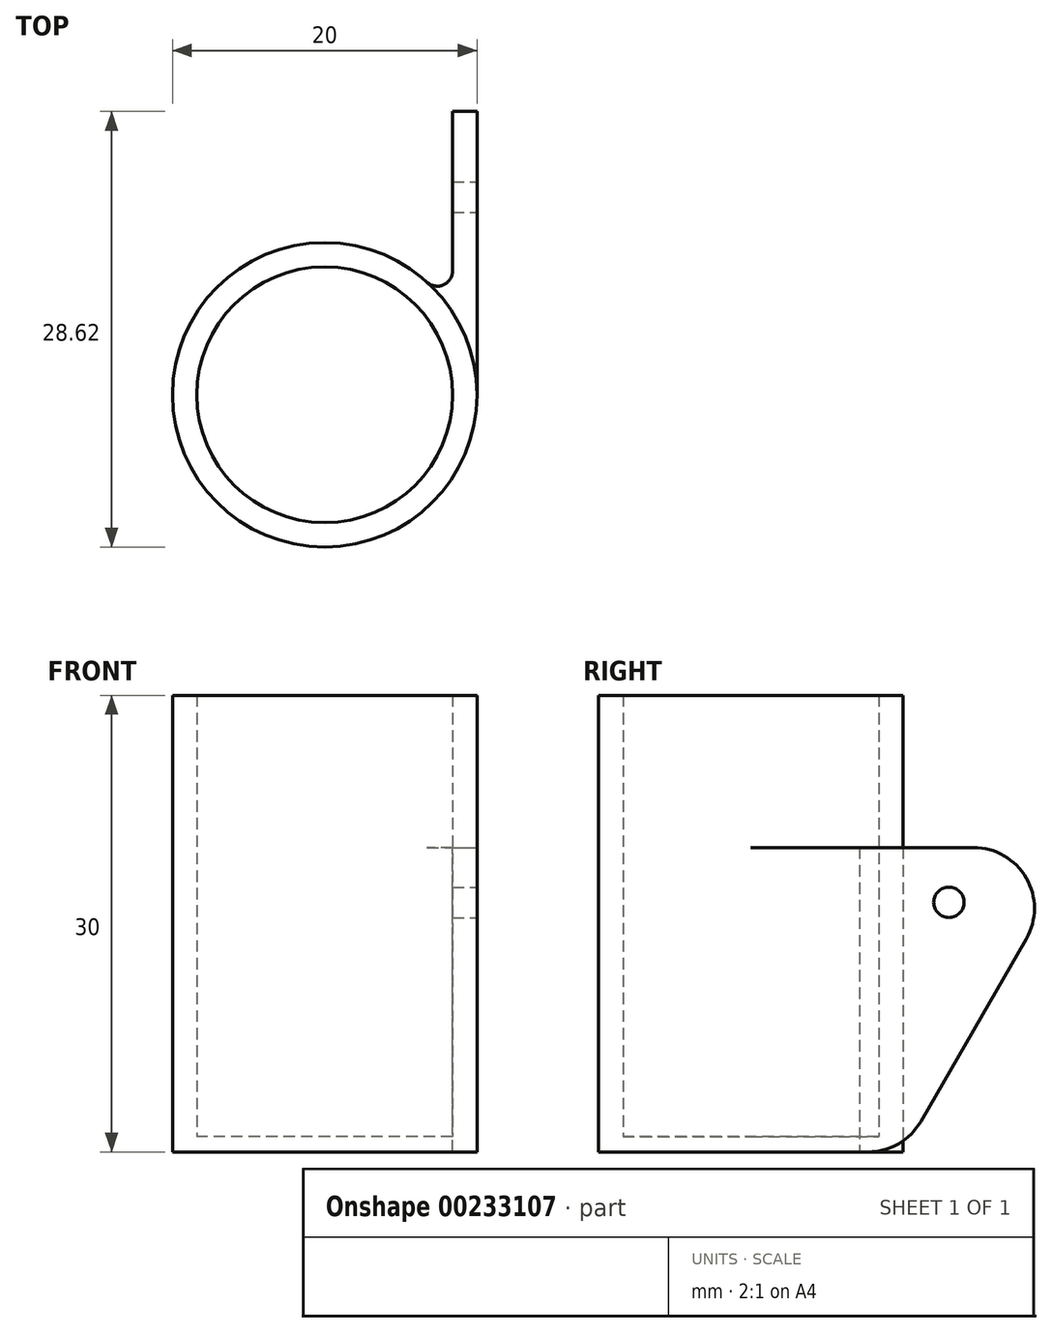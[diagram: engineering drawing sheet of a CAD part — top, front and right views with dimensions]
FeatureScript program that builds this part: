
annotation { "Feature Type Name" : "Feature", "Feature Type Description" : "" }
export const myFeature = defineFeature(function(context is Context, id is Id, definition is map)
    precondition{}
    {
        {
            var Q0;
            Q0=qCreatedBy(makeId("Top.planeOp"),FACE);
            var sketch = newSketch(context, id + "F0", { "sketchPlane" : qUnion([Q0])});
            skCircle(sketch, "E0", {"center": v(0, 0) * mm, "radius": 10 * mm});
            skSolve(sketch);
        }
        {
            var Q0;
            Q0 = qSketchRegion(id + "F0", true);
            extrude(context, id + "F1", {"entities" : qUnion([Q0]), "depth" : 1 * mm});
        }
        {
            var Q0;
            Q0=makeQuery(id+"F1.opExtrude","CAP_FACE",FACE,{"disambiguationData":[OSD([sQuery(id+"F0.wireOp",EDGE,"E0")])],"isStart":false});
            var sketch = newSketch(context, id + "F2", { "sketchPlane" : qUnion([Q0])});
            skCircle(sketch, "E1.0", {"center": v(0, 0) * mm, "radius": 10 * mm});
            skCircle(sketch, "E2.0", {"center": v(0, 0) * mm, "radius": 8.4 * mm});
            skSolve(sketch);
        }
        {
            var Q0;
            Q0 = qSketchRegion(id + "F2", true);
            extrude(context, id + "F3", {"entities" : qUnion([Q0]), "operationType" : NewBodyOperationType.ADD, "depth" : 29 * mm});
        }
        {
            var Q0;
            Q0=qCreatedBy(makeId("Right.planeOp"),FACE);
            cPlane(context, id + "F4", {"entities" : qUnion([Q0]), "cplaneType" : CPlaneType.OFFSET, "offset" : 10 * mm, "width" : 150 * mm, "height" : 150 * mm});
        }
        {
            var Q0;
            Q0=qCreatedBy(id+"F4.planeOp",FACE);
            var sketch = newSketch(context, id + "F5", { "sketchPlane" : qUnion([Q0])});
            skLineSegment(sketch, "E3", {"start": v(0, 0) * mm, "end": v(10, 0) * mm});
            skLineSegment(sketch, "E4", {"start": v(0, 0) * mm, "end": v(0, 20) * mm});
            skLineSegment(sketch, "E5", {"start": v(10, 0) * mm, "end": v(21.55, 20) * mm});
            skLineSegment(sketch, "E6", {"start": v(0, 20) * mm, "end": v(21.55, 20) * mm});
            skSolve(sketch);
        }
        {
            var Q0;
            Q0 = qSketchRegion(id + "F5", true);
            extrude(context, id + "F6", {"entities" : qUnion([Q0]), "operationType" : NewBodyOperationType.ADD, "oppositeDirection" : true, "depth" : 1.6 * mm});
        }
        {
            var Q0;
            Q0=makeQuery(id+"F6.opExtrude","CAP_FACE",FACE,{"disambiguationData":[OSD([sQuery(id+"F5.wireOp",EDGE,"E3"),sQuery(id+"F5.wireOp",EDGE,"E4"),sQuery(id+"F5.wireOp",EDGE,"E5"),sQuery(id+"F5.wireOp",EDGE,"E6")])],"isStart":true});
            var sketch = newSketch(context, id + "F7", { "sketchPlane" : qUnion([Q0])});
            skCircle(sketch, "E7", {"center": v(13, 16.4) * mm, "radius": 1 * mm});
            skSolve(sketch);
        }
        {
            var Q0;
            Q0 = qSketchRegion(id + "F7", true);
            extrude(context, id + "F8", {"entities" : qUnion([Q0]), "operationType" : NewBodyOperationType.REMOVE, "endBound" : BoundingType.UP_TO_NEXT, "oppositeDirection" : true, "depth" : 25 * mm});
        }
        {
            var Q0;
            Q0=makeQuery(id+"F6.opExtrude","SWEPT_EDGE",EDGE,{"disambiguationData":[OSD([sQuery(id+"F5.wireOp",EDGE,"E5"),sQuery(id+"F5.wireOp",EDGE,"E6")])]});
            var Q1;
            Q1=makeQuery(id+"F6.opExtrude","SWEPT_EDGE",EDGE,{"disambiguationData":[OSD([sQuery(id+"F5.wireOp",EDGE,"E3"),sQuery(id+"F5.wireOp",EDGE,"E5")])]});
            fillet(context, id + "F9", {"entities" : qUnion([Q0, Q1]), "radius" : 4 * mm, "tangentPropagation" : true, "allowEdgeOverflow" : false});
        }
        {
            var Q0;
            Q0=makeQuery(id+"F6.boolean.opBoolean","INTERSECT",EDGE,{"derivedFrom":[makeQuery(id+"F3.boolean.opBoolean","MERGE",FACE,{"derivedFrom":[makeQuery(id+"F1.opExtrude","SWEPT_FACE",FACE,{"disambiguationData":[OSD([sQuery(id+"F0.wireOp",EDGE,"E0")])]}),makeQuery(id+"F3.opExtrude","SWEPT_FACE",FACE,{"disambiguationData":[OSD([sQuery(id+"F2.wireOp",EDGE,"E1.0")])]})]}),makeQuery(id+"F6.opExtrude","CAP_FACE",FACE,{"disambiguationData":[OSD([sQuery(id+"F5.wireOp",EDGE,"E3"),sQuery(id+"F5.wireOp",EDGE,"E4"),sQuery(id+"F5.wireOp",EDGE,"E5"),sQuery(id+"F5.wireOp",EDGE,"E6")])],"isStart":false})]});
            fillet(context, id + "F10", {"entities" : qUnion([Q0]), "radius" : 1 * mm, "tangentPropagation" : true, "allowEdgeOverflow" : false});
        }
    });
